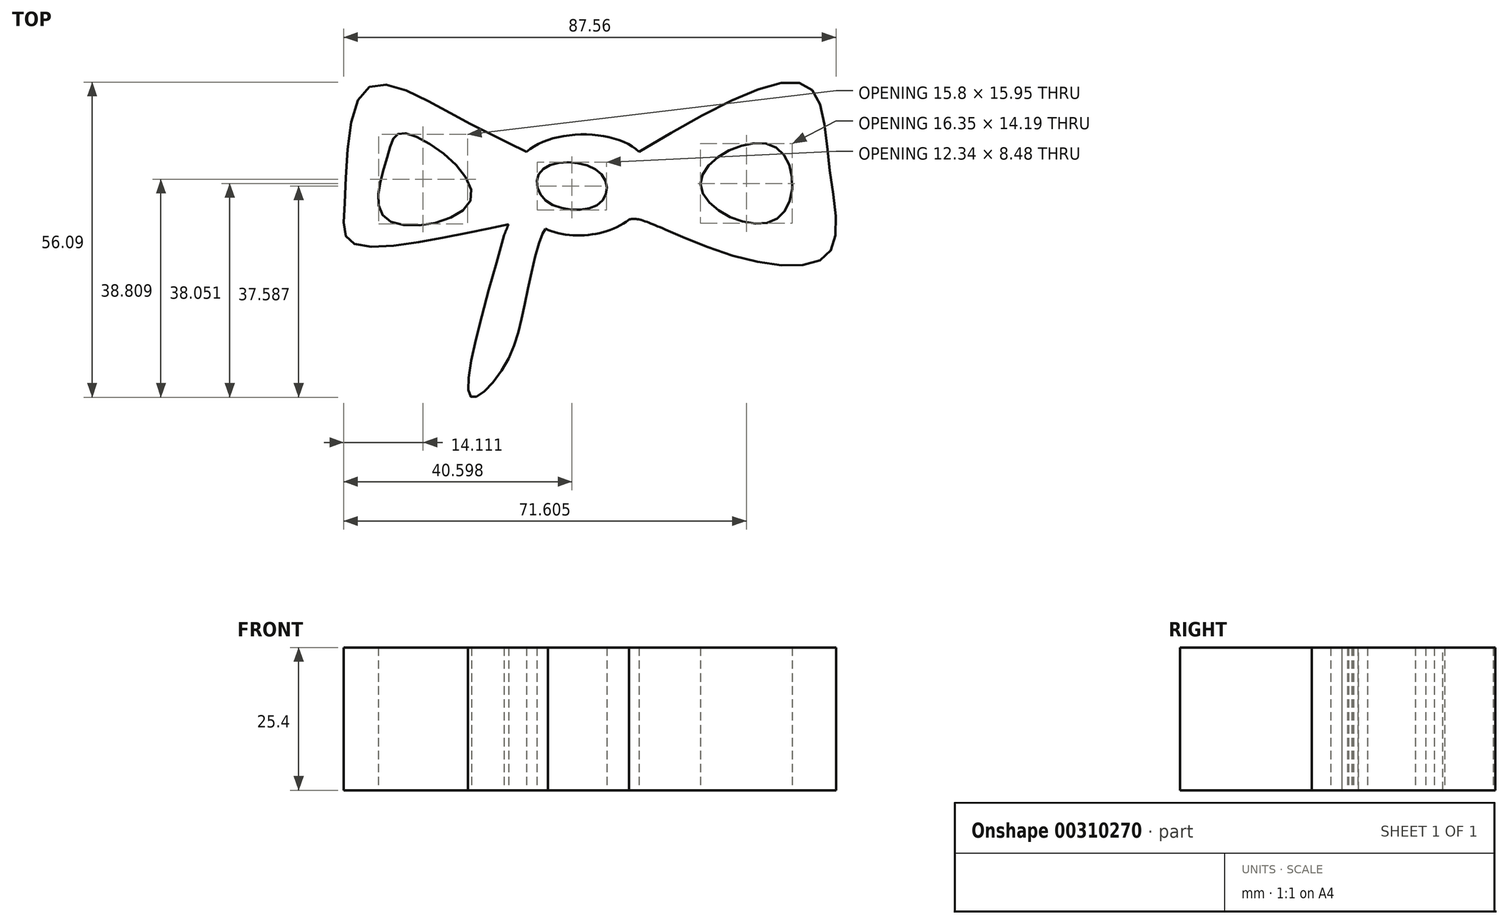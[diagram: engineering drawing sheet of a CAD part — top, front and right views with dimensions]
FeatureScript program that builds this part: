
annotation { "Feature Type Name" : "Feature", "Feature Type Description" : "" }
export const myFeature = defineFeature(function(context is Context, id is Id, definition is map)
    precondition{}
    {
        {
            var Q0;
            Q0=qCreatedBy(makeId("Top.planeOp"),FACE);
            var sketch = newSketch(context, id + "F0", { "sketchPlane" : qUnion([Q0])});
            skFitSpline(sketch, "E0", {"points": [v(-13.02, 12.04) * mm, v(7, 12.04) * mm, v(5.18, 0) * mm, v(-12.4, 0) * mm, v(-13.02, 12.04) * mm]});
            skFitSpline(sketch, "E1", {"points": [v(7, 12.04) * mm, v(36.58, 23.92) * mm, v(40.84, 9.3) * mm, v(40.54, -6.25) * mm, v(23.15, -6.27) * mm, v(7, 0) * mm, v(5.18, 0) * mm], "startDerivative": vector(151.11, 89.14) * mm, "endDerivative": vector(-24.52, -5.17) * mm});
            skFitSpline(sketch, "E2", {"points": [v(-13.02, 12.04) * mm, v(-27.34, 19.35) * mm, v(-41.37, 23.32) * mm, v(-45.33, 3.5) * mm, v(-44.1, -4.12) * mm, v(-27.65, -3.2) * mm, v(-12.4, 0) * mm], "startDerivative": vector(-77.73, 37.93) * mm, "endDerivative": vector(81.33, 17.97) * mm});
            skFitSpline(sketch, "E3", {"points": [v(11.65, -1.77) * mm, v(13.73, -7.12) * mm, v(18.82, -29.15) * mm, v(14.64, -30.48) * mm, v(5.18, 0) * mm, v(5.18, -2.55) * mm, v(5.18, -2.33) * mm], "startDerivative": vector(6.7, -26.26) * mm, "endDerivative": vector(-0.4, 17.56) * mm});
            skFitSpline(sketch, "E4", {"points": [v(-10.06, 8.99) * mm, v(0, 8.38) * mm, v(0, 2.9) * mm, v(-9.75, 3.5) * mm, v(-10.06, 8.99) * mm]});
            skFitSpline(sketch, "E5", {"points": [v(-37.8, 11.12) * mm, v(-37.8, 0) * mm, v(-22.85, 3.8) * mm, v(-34.75, 15.4) * mm, v(-37.8, 11.12) * mm]});
            skFitSpline(sketch, "E6", {"points": [v(17.9, 6.3) * mm, v(31.09, 12.95) * mm, v(31.3, 0) * mm, v(17.9, 6.3) * mm]});
            skFitSpline(sketch, "E7", {"points": [v(-17.04, -2.84) * mm, v(-22.85, -31.54) * mm, v(-17.04, -26.25) * mm, v(-12.76, -12.15) * mm, v(-9.66, -1.7) * mm, v(-9.22, -1.87) * mm], "startDerivative": vector(-31.88, -116.17) * mm, "endDerivative": vector(10.04, -8.23) * mm});
            skFitSpline(sketch, "E8", {"points": [v(-17.04, -2.84) * mm, v(-16.22, -0.84) * mm], "startDerivative": vector(0.8, 2.04) * mm, "endDerivative": vector(0.8, 2.04) * mm});
            skSolve(sketch);
        }
        {
            var Q0;
            Q0=makeQuery(id+"F0.imprint","IMPRINT",FACE,{"disambiguationData":[TD([[makeQuery(id+"F0.imprint","IMPRINT",EDGE,{"derivedFrom":sQuery(id+"F0.wireOp",EDGE,"E5")}),-1.0]])]});
            var Q1;
            {var subQ5=sQuery(id+"F0.wireOp",EDGE,"E8");Q1=makeQuery(id+"F0.imprint","IMPRINT",FACE,{"disambiguationData":[TD([[makeQuery(id+"F0.imprint","IMPRINT",EDGE,{"derivedFrom":subQ5}),-1.0]])]});}
            var Q2;
            Q2=makeQuery(id+"F0.imprint","IMPRINT",FACE,{"disambiguationData":[TD([[makeQuery(id+"F0.imprint","IMPRINT",EDGE,{"derivedFrom":sQuery(id+"F0.wireOp",EDGE,"E6")}),1.0]])]});
            var Q3;
            Q3=makeQuery(id+"F0.imprint","IMPRINT",FACE,{"disambiguationData":[TD([[makeQuery(id+"F0.imprint","IMPRINT",EDGE,{"derivedFrom":sQuery(id+"F0.wireOp",EDGE,"E4")}),1.0]])]});
            var Q4;
            {var subQ0=sQuery(id+"F0.wireOp",EDGE,"E3");var subQ1=sQuery(id+"F0.wireOp",EDGE,"E1");var subQ2=makeQuery(id+"F0.imprint","INTERSECT",VERTEX,{"disambiguationData":[OD(0.0)],"derivedFrom":[subQ1,subQ0]});Q4=makeQuery(id+"F0.imprint","IMPRINT",FACE,{"disambiguationData":[TD([[makeQuery(id+"F0.imprint","IMPRINT",EDGE,{"disambiguationData":[TD([[subQ2,-1.0]])],"derivedFrom":subQ1}),1.0]])]});}
            extrude(context, id + "F1", {"entities" : qUnion([Q0, Q1, Q2, Q3, Q4]), "depth" : 25.4 * mm});
        }
    });
